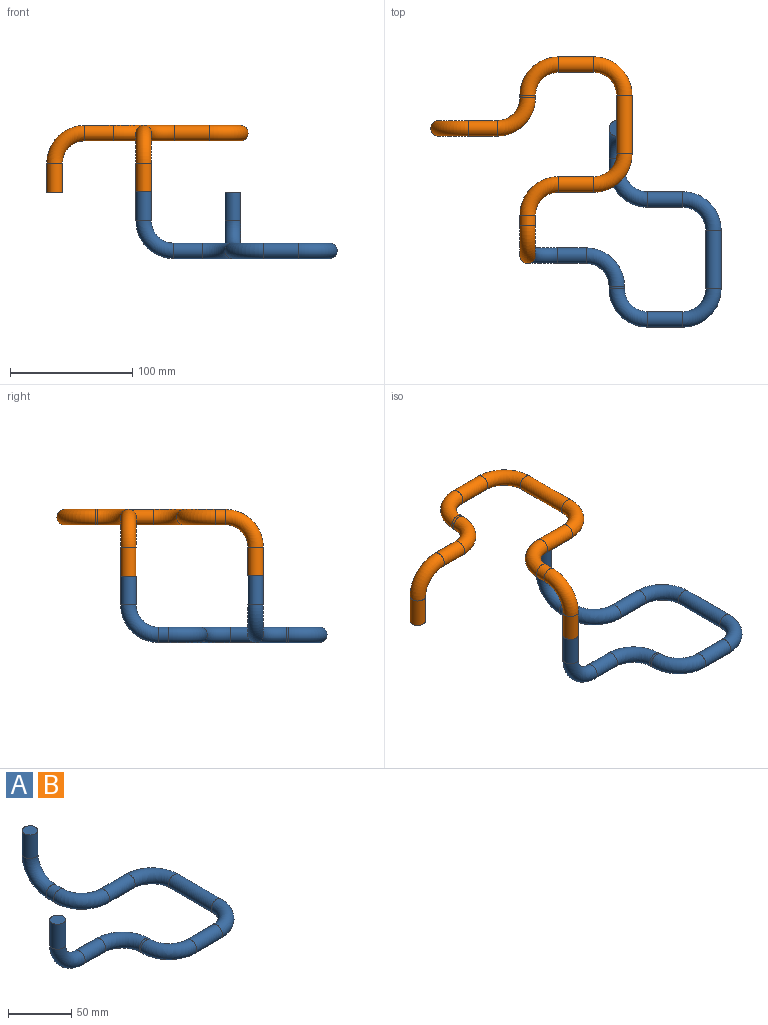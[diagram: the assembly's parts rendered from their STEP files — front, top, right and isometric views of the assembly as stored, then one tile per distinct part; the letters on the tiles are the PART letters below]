
ASSEMBLY  parts=2 mates=1
PART A: 17 faces, bbox 169.4x173.6x57.6 mm
  f0: plane 12.66x12.66mm, normal (0,0,1), area 125.9mm2, adj f2
  f1: plane 12.66x12.66mm, normal (0,0,1), area 125.9mm2, adj f16
  f2: cylinder r=6.33mm len=22.86mm, axis (0,0,-1), area 909.5mm2, adj f0,f3
  f3: torus R=24.42mm, axis (-1,0,0), area 1526mm2, adj f2,f4
  f4: cylinder r=6.33mm len=12.66mm, axis (0,-1,0), area 338.9mm2, adj f3,f5
  f5: torus R=25mm, axis (0,0,1), area 1562.3mm2, adj f4,f6
  f6: cylinder r=6.33mm len=28.87mm, axis (1,0,0), area 1148.4mm2, adj f5,f7
  f7: torus R=25mm, axis (0,0,-1), area 1562.3mm2, adj f6,f8
  f8: cylinder r=6.33mm len=47.84mm, axis (0,-1,0), area 1903.2mm2, adj f7,f9
  f9: torus R=25mm, axis (0,0,-1), area 1562.3mm2, adj f8,f10
  f10: cylinder r=6.33mm len=28.87mm, axis (-1,0,0), area 1148.4mm2, adj f9,f11
  f11: torus R=25mm, axis (0,0,-1), area 1562.3mm2, adj f10,f12
  f12: cylinder r=6.33mm len=12.66mm, axis (0,1,0), area 79.8mm2, adj f11,f13
  f13: torus R=25mm, axis (0,0,1), area 1562.3mm2, adj f12,f14
  f14: cylinder r=6.33mm len=23.3mm, axis (-1,0,0), area 927mm2, adj f13,f15
  f15: torus R=24.42mm, axis (0,1,0), area 1526mm2, adj f14,f16
  f16: cylinder r=6.33mm len=24.35mm, axis (0,0,1), area 968.7mm2, adj f1,f15
PART B: same geometry as A
PLACE A t=(-29.92,96.37,-110.26)mm
PLACE B rot(axis=(1,0,0),180deg) t=(-102.64,150.52,-13.05)mm
MATE revolute B.f2 <-> A.f16  axis (0,0,-1) through (-102.64,71.56,-60.91)mm
